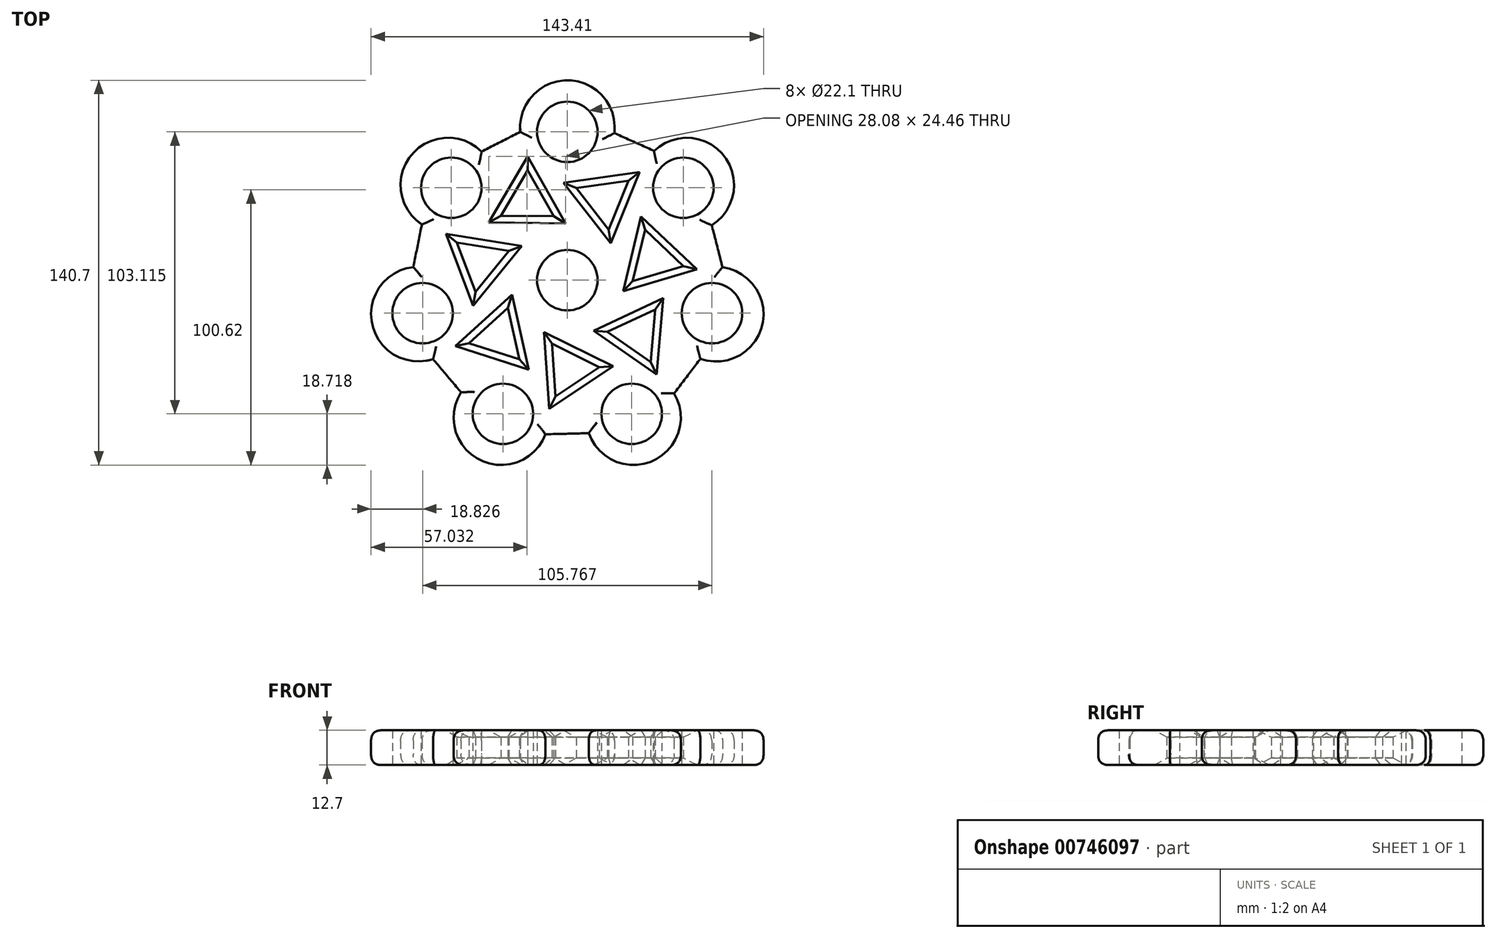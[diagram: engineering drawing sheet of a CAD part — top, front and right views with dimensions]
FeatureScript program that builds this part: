
annotation { "Feature Type Name" : "Feature", "Feature Type Description" : "" }
export const myFeature = defineFeature(function(context is Context, id is Id, definition is map)
    precondition{}
    {
        {
            var Q0;
            Q0=qCreatedBy(makeId("Top.planeOp"),FACE);
            var sketch = newSketch(context, id + "F0", { "sketchPlane" : qUnion([Q0])});
            skCircle(sketch, "E0", {"center": v(0, 0) * mm, "radius": 11.05 * mm});
            skCircle(sketch, "E1", {"center": v(0, 54.24) * mm, "radius": 11.05 * mm});
            skCircle(sketch, "E2.1.0", {"center": v(-42.4, 33.82) * mm, "radius": 11.05 * mm});
            skCircle(sketch, "E2.2.0", {"center": v(-52.88, -12.07) * mm, "radius": 11.05 * mm});
            skCircle(sketch, "E2.3.0", {"center": v(-23.54, -48.87) * mm, "radius": 11.05 * mm});
            skCircle(sketch, "E2.4.0", {"center": v(23.54, -48.87) * mm, "radius": 11.05 * mm});
            skCircle(sketch, "E2.5.0", {"center": v(52.88, -12.07) * mm, "radius": 11.05 * mm});
            skCircle(sketch, "E2.6.0", {"center": v(42.4, 33.82) * mm, "radius": 11.05 * mm});
            skArc(sketch, "E3", {"start": v(17.2, 53.8) * mm, "mid": v(0.24, 73.1) * mm, "end": v(-17.2, 54.24) * mm});
            skArc(sketch, "E4.1.0", {"start": v(-31.34, 47) * mm, "mid": v(-57, 45.77) * mm, "end": v(-53.14, 20.37) * mm});
            skArc(sketch, "E4.2.0", {"start": v(-56.29, 4.8) * mm, "mid": v(-71.33, -16.03) * mm, "end": v(-49.05, -28.85) * mm});
            skArc(sketch, "E4.3.0", {"start": v(-38.85, -41.01) * mm, "mid": v(-31.94, -65.76) * mm, "end": v(-8.03, -56.34) * mm});
            skArc(sketch, "E4.4.0", {"start": v(7.84, -55.95) * mm, "mid": v(31.5, -65.97) * mm, "end": v(39.04, -41.4) * mm});
            skArc(sketch, "E4.5.0", {"start": v(48.63, -28.75) * mm, "mid": v(71.22, -16.5) * mm, "end": v(56.71, 4.7) * mm});
            skArc(sketch, "E4.6.0", {"start": v(52.8, 20.1) * mm, "mid": v(57.3, 45.4) * mm, "end": v(31.68, 47.28) * mm});
            skLineSegment(sketch, "E5", {"start": v(-31.34, 47) * mm, "end": v(-17.2, 54.24) * mm});
            skLineSegment(sketch, "E6.1.0", {"start": v(-56.29, 4.8) * mm, "end": v(-53.14, 20.37) * mm});
            skLineSegment(sketch, "E6.2.0", {"start": v(-38.85, -41.01) * mm, "end": v(-49.05, -28.85) * mm});
            skLineSegment(sketch, "E6.3.0", {"start": v(7.84, -55.95) * mm, "end": v(-8.03, -56.34) * mm});
            skLineSegment(sketch, "E6.4.0", {"start": v(48.63, -28.75) * mm, "end": v(39.04, -41.4) * mm});
            skLineSegment(sketch, "E6.5.0", {"start": v(52.8, 20.1) * mm, "end": v(56.71, 4.7) * mm});
            skLineSegment(sketch, "E6.6.0", {"start": v(17.2, 53.8) * mm, "end": v(31.68, 47.28) * mm});
            skCircle(sketch, "E7.cCircle", {"center": v(-14.6, 29.05) * mm, "radius": 11.13 * mm, "construction": true});
            skLineSegment(sketch, "E7.0", {"start": v(-5.01, 23.38) * mm, "end": v(-24.3, 23.58) * mm});
            skLineSegment(sketch, "E7.1", {"start": v(-24.3, 23.58) * mm, "end": v(-14.48, 40.18) * mm});
            skLineSegment(sketch, "E7.2", {"start": v(-14.48, 40.18) * mm, "end": v(-5.01, 23.38) * mm});
            skLineSegment(sketch, "E8.1.0", {"start": v(-40.44, 13.73) * mm, "end": v(-21.4, 10.66) * mm});
            skLineSegment(sketch, "E8.1.1", {"start": v(-33.58, -4.3) * mm, "end": v(-40.44, 13.73) * mm});
            skLineSegment(sketch, "E8.1.2", {"start": v(-21.4, 10.66) * mm, "end": v(-33.58, -4.3) * mm});
            skLineSegment(sketch, "E8.2.0", {"start": v(-35.95, -23.06) * mm, "end": v(-21.68, -10.09) * mm});
            skLineSegment(sketch, "E8.2.1", {"start": v(-17.58, -28.93) * mm, "end": v(-35.95, -23.06) * mm});
            skLineSegment(sketch, "E8.2.2", {"start": v(-21.68, -10.09) * mm, "end": v(-17.58, -28.93) * mm});
            skLineSegment(sketch, "E8.3.0", {"start": v(-4.39, -42.49) * mm, "end": v(-5.63, -23.24) * mm});
            skLineSegment(sketch, "E8.3.1", {"start": v(11.66, -31.78) * mm, "end": v(-4.39, -42.49) * mm});
            skLineSegment(sketch, "E8.3.2", {"start": v(-5.63, -23.24) * mm, "end": v(11.66, -31.78) * mm});
            skLineSegment(sketch, "E8.4.0", {"start": v(30.48, -29.92) * mm, "end": v(14.66, -18.9) * mm});
            skLineSegment(sketch, "E8.4.1", {"start": v(32.12, -10.7) * mm, "end": v(30.48, -29.92) * mm});
            skLineSegment(sketch, "E8.4.2", {"start": v(14.66, -18.9) * mm, "end": v(32.12, -10.7) * mm});
            skLineSegment(sketch, "E8.5.0", {"start": v(42.4, 5.18) * mm, "end": v(23.91, -0.32) * mm});
            skLineSegment(sketch, "E8.5.1", {"start": v(28.4, 18.44) * mm, "end": v(42.4, 5.18) * mm});
            skLineSegment(sketch, "E8.5.2", {"start": v(23.91, -0.32) * mm, "end": v(28.4, 18.44) * mm});
            skLineSegment(sketch, "E8.6.0", {"start": v(22.38, 36.38) * mm, "end": v(15.16, 18.5) * mm});
            skLineSegment(sketch, "E8.6.1", {"start": v(3.29, 33.7) * mm, "end": v(22.38, 36.38) * mm});
            skLineSegment(sketch, "E8.6.2", {"start": v(15.16, 18.5) * mm, "end": v(3.29, 33.7) * mm});
            skSolve(sketch);
        }
        {
            var Q0;
            Q0=makeQuery(id+"F0.imprint","IMPRINT",FACE,{"disambiguationData":[TD([[makeQuery(id+"F0.imprint","IMPRINT",EDGE,{"derivedFrom":sQuery(id+"F0.wireOp",EDGE,"E0")}),-1.0]])]});
            extrude(context, id + "F1", {"entities" : qUnion([Q0]), "depth" : 12.7 * mm, "offsetDistance" : 25.4 * mm});
        }
        {
            var Q0;
            Q0=makeQuery(id+"F1.opExtrude","CAP_EDGE",EDGE,{"disambiguationData":[OSD([sQuery(id+"F0.wireOp",EDGE,"E6.3.0")])],"isStart":false});
            var Q1;
            Q1=makeQuery(id+"F1.opExtrude","CAP_EDGE",EDGE,{"disambiguationData":[OSD([sQuery(id+"F0.wireOp",EDGE,"E4.4.0")])],"isStart":false});
            var Q2;
            Q2=makeQuery(id+"F1.opExtrude","CAP_EDGE",EDGE,{"disambiguationData":[OSD([sQuery(id+"F0.wireOp",EDGE,"E6.4.0")])],"isStart":false});
            var Q3;
            Q3=makeQuery(id+"F1.opExtrude","CAP_EDGE",EDGE,{"disambiguationData":[OSD([sQuery(id+"F0.wireOp",EDGE,"E4.5.0")])],"isStart":false});
            var Q4;
            Q4=makeQuery(id+"F1.opExtrude","CAP_EDGE",EDGE,{"disambiguationData":[OSD([sQuery(id+"F0.wireOp",EDGE,"E6.5.0")])],"isStart":false});
            var Q5;
            Q5=makeQuery(id+"F1.opExtrude","CAP_EDGE",EDGE,{"disambiguationData":[OSD([sQuery(id+"F0.wireOp",EDGE,"E4.6.0")])],"isStart":false});
            var Q6;
            Q6=makeQuery(id+"F1.opExtrude","CAP_EDGE",EDGE,{"disambiguationData":[OSD([sQuery(id+"F0.wireOp",EDGE,"E6.6.0")])],"isStart":false});
            var Q7;
            Q7=makeQuery(id+"F1.opExtrude","CAP_EDGE",EDGE,{"disambiguationData":[OSD([sQuery(id+"F0.wireOp",EDGE,"E3")])],"isStart":false});
            var Q8;
            Q8=makeQuery(id+"F1.opExtrude","CAP_EDGE",EDGE,{"disambiguationData":[OSD([sQuery(id+"F0.wireOp",EDGE,"E5")])],"isStart":false});
            var Q9;
            Q9=makeQuery(id+"F1.opExtrude","CAP_EDGE",EDGE,{"disambiguationData":[OSD([sQuery(id+"F0.wireOp",EDGE,"E4.1.0")])],"isStart":false});
            var Q10;
            Q10=makeQuery(id+"F1.opExtrude","CAP_EDGE",EDGE,{"disambiguationData":[OSD([sQuery(id+"F0.wireOp",EDGE,"E6.1.0")])],"isStart":false});
            var Q11;
            Q11=makeQuery(id+"F1.opExtrude","CAP_EDGE",EDGE,{"disambiguationData":[OSD([sQuery(id+"F0.wireOp",EDGE,"E4.2.0")])],"isStart":false});
            var Q12;
            Q12=makeQuery(id+"F1.opExtrude","CAP_EDGE",EDGE,{"disambiguationData":[OSD([sQuery(id+"F0.wireOp",EDGE,"E6.2.0")])],"isStart":false});
            var Q13;
            Q13=makeQuery(id+"F1.opExtrude","CAP_EDGE",EDGE,{"disambiguationData":[OSD([sQuery(id+"F0.wireOp",EDGE,"E4.3.0")])],"isStart":false});
            var Q14;
            Q14=makeQuery(id+"F1.opExtrude","CAP_EDGE",EDGE,{"disambiguationData":[OSD([sQuery(id+"F0.wireOp",EDGE,"E3")])],"isStart":true});
            var Q15;
            Q15=makeQuery(id+"F1.opExtrude","CAP_EDGE",EDGE,{"disambiguationData":[OSD([sQuery(id+"F0.wireOp",EDGE,"E6.6.0")])],"isStart":true});
            var Q16;
            Q16=makeQuery(id+"F1.opExtrude","CAP_EDGE",EDGE,{"disambiguationData":[OSD([sQuery(id+"F0.wireOp",EDGE,"E4.6.0")])],"isStart":true});
            var Q17;
            Q17=makeQuery(id+"F1.opExtrude","CAP_EDGE",EDGE,{"disambiguationData":[OSD([sQuery(id+"F0.wireOp",EDGE,"E6.5.0")])],"isStart":true});
            var Q18;
            Q18=makeQuery(id+"F1.opExtrude","CAP_EDGE",EDGE,{"disambiguationData":[OSD([sQuery(id+"F0.wireOp",EDGE,"E4.5.0")])],"isStart":true});
            var Q19;
            Q19=makeQuery(id+"F1.opExtrude","CAP_EDGE",EDGE,{"disambiguationData":[OSD([sQuery(id+"F0.wireOp",EDGE,"E6.4.0")])],"isStart":true});
            var Q20;
            Q20=makeQuery(id+"F1.opExtrude","CAP_EDGE",EDGE,{"disambiguationData":[OSD([sQuery(id+"F0.wireOp",EDGE,"E4.4.0")])],"isStart":true});
            var Q21;
            Q21=makeQuery(id+"F1.opExtrude","CAP_EDGE",EDGE,{"disambiguationData":[OSD([sQuery(id+"F0.wireOp",EDGE,"E4.3.0")])],"isStart":true});
            var Q22;
            Q22=makeQuery(id+"F1.opExtrude","CAP_EDGE",EDGE,{"disambiguationData":[OSD([sQuery(id+"F0.wireOp",EDGE,"E6.3.0")])],"isStart":true});
            var Q23;
            Q23=makeQuery(id+"F1.opExtrude","CAP_EDGE",EDGE,{"disambiguationData":[OSD([sQuery(id+"F0.wireOp",EDGE,"E6.2.0")])],"isStart":true});
            var Q24;
            Q24=makeQuery(id+"F1.opExtrude","CAP_EDGE",EDGE,{"disambiguationData":[OSD([sQuery(id+"F0.wireOp",EDGE,"E4.2.0")])],"isStart":true});
            var Q25;
            Q25=makeQuery(id+"F1.opExtrude","CAP_EDGE",EDGE,{"disambiguationData":[OSD([sQuery(id+"F0.wireOp",EDGE,"E4.1.0")])],"isStart":true});
            var Q26;
            Q26=makeQuery(id+"F1.opExtrude","CAP_EDGE",EDGE,{"disambiguationData":[OSD([sQuery(id+"F0.wireOp",EDGE,"E6.1.0")])],"isStart":true});
            var Q27;
            Q27=makeQuery(id+"F1.opExtrude","CAP_EDGE",EDGE,{"disambiguationData":[OSD([sQuery(id+"F0.wireOp",EDGE,"E5")])],"isStart":true});
            fillet(context, id + "F2", {"entities" : qUnion([Q0, Q1, Q2, Q3, Q4, Q5, Q6, Q7, Q8, Q9, Q10, Q11, Q12, Q13, Q14, Q15, Q16, Q17, Q18, Q19, Q20, Q21, Q22, Q23, Q24, Q25, Q26, Q27]), "radius" : 3.8 * mm, "tangentPropagation" : true, "rho" : 0.5, "crossSection" : FilletCrossSection.CONIC, "allowEdgeOverflow" : false});
        }
        {
            var Q0;
            Q0=makeQuery(id+"F1.opExtrude","CAP_EDGE",EDGE,{"disambiguationData":[OSD([sQuery(id+"F0.wireOp",EDGE,"E8.1.0")])],"isStart":false});
            var Q1;
            Q1=makeQuery(id+"F1.opExtrude","CAP_EDGE",EDGE,{"disambiguationData":[OSD([sQuery(id+"F0.wireOp",EDGE,"E8.1.2")])],"isStart":false});
            var Q2;
            Q2=makeQuery(id+"F1.opExtrude","CAP_EDGE",EDGE,{"disambiguationData":[OSD([sQuery(id+"F0.wireOp",EDGE,"E8.1.1")])],"isStart":false});
            var Q3;
            Q3=makeQuery(id+"F1.opExtrude","CAP_EDGE",EDGE,{"disambiguationData":[OSD([sQuery(id+"F0.wireOp",EDGE,"E7.2")])],"isStart":false});
            var Q4;
            Q4=makeQuery(id+"F1.opExtrude","CAP_EDGE",EDGE,{"disambiguationData":[OSD([sQuery(id+"F0.wireOp",EDGE,"E7.1")])],"isStart":false});
            var Q5;
            Q5=makeQuery(id+"F1.opExtrude","CAP_EDGE",EDGE,{"disambiguationData":[OSD([sQuery(id+"F0.wireOp",EDGE,"E7.0")])],"isStart":false});
            var Q6;
            Q6=makeQuery(id+"F1.opExtrude","CAP_EDGE",EDGE,{"disambiguationData":[OSD([sQuery(id+"F0.wireOp",EDGE,"E8.6.1")])],"isStart":false});
            var Q7;
            Q7=makeQuery(id+"F1.opExtrude","CAP_EDGE",EDGE,{"disambiguationData":[OSD([sQuery(id+"F0.wireOp",EDGE,"E8.6.0")])],"isStart":false});
            var Q8;
            Q8=makeQuery(id+"F1.opExtrude","CAP_EDGE",EDGE,{"disambiguationData":[OSD([sQuery(id+"F0.wireOp",EDGE,"E8.6.2")])],"isStart":false});
            var Q9;
            Q9=makeQuery(id+"F1.opExtrude","CAP_EDGE",EDGE,{"disambiguationData":[OSD([sQuery(id+"F0.wireOp",EDGE,"E8.5.2")])],"isStart":false});
            var Q10;
            Q10=makeQuery(id+"F1.opExtrude","CAP_EDGE",EDGE,{"disambiguationData":[OSD([sQuery(id+"F0.wireOp",EDGE,"E8.5.1")])],"isStart":false});
            var Q11;
            Q11=makeQuery(id+"F1.opExtrude","CAP_EDGE",EDGE,{"disambiguationData":[OSD([sQuery(id+"F0.wireOp",EDGE,"E8.5.0")])],"isStart":false});
            var Q12;
            Q12=makeQuery(id+"F1.opExtrude","CAP_EDGE",EDGE,{"disambiguationData":[OSD([sQuery(id+"F0.wireOp",EDGE,"E8.4.2")])],"isStart":false});
            var Q13;
            Q13=makeQuery(id+"F1.opExtrude","CAP_EDGE",EDGE,{"disambiguationData":[OSD([sQuery(id+"F0.wireOp",EDGE,"E8.4.1")])],"isStart":false});
            var Q14;
            Q14=makeQuery(id+"F1.opExtrude","CAP_EDGE",EDGE,{"disambiguationData":[OSD([sQuery(id+"F0.wireOp",EDGE,"E8.4.0")])],"isStart":false});
            var Q15;
            Q15=makeQuery(id+"F1.opExtrude","CAP_EDGE",EDGE,{"disambiguationData":[OSD([sQuery(id+"F0.wireOp",EDGE,"E8.3.1")])],"isStart":false});
            var Q16;
            Q16=makeQuery(id+"F1.opExtrude","CAP_EDGE",EDGE,{"disambiguationData":[OSD([sQuery(id+"F0.wireOp",EDGE,"E8.3.2")])],"isStart":false});
            var Q17;
            Q17=makeQuery(id+"F1.opExtrude","CAP_EDGE",EDGE,{"disambiguationData":[OSD([sQuery(id+"F0.wireOp",EDGE,"E8.3.0")])],"isStart":false});
            var Q18;
            Q18=makeQuery(id+"F1.opExtrude","CAP_EDGE",EDGE,{"disambiguationData":[OSD([sQuery(id+"F0.wireOp",EDGE,"E8.2.1")])],"isStart":false});
            var Q19;
            Q19=makeQuery(id+"F1.opExtrude","CAP_EDGE",EDGE,{"disambiguationData":[OSD([sQuery(id+"F0.wireOp",EDGE,"E8.2.0")])],"isStart":false});
            var Q20;
            Q20=makeQuery(id+"F1.opExtrude","CAP_EDGE",EDGE,{"disambiguationData":[OSD([sQuery(id+"F0.wireOp",EDGE,"E8.2.2")])],"isStart":false});
            var Q21;
            Q21=makeQuery(id+"F1.opExtrude","CAP_EDGE",EDGE,{"disambiguationData":[OSD([sQuery(id+"F0.wireOp",EDGE,"E8.3.2")])],"isStart":true});
            var Q22;
            Q22=makeQuery(id+"F1.opExtrude","CAP_EDGE",EDGE,{"disambiguationData":[OSD([sQuery(id+"F0.wireOp",EDGE,"E8.3.0")])],"isStart":true});
            var Q23;
            Q23=makeQuery(id+"F1.opExtrude","CAP_EDGE",EDGE,{"disambiguationData":[OSD([sQuery(id+"F0.wireOp",EDGE,"E8.3.1")])],"isStart":true});
            var Q24;
            Q24=makeQuery(id+"F1.opExtrude","CAP_EDGE",EDGE,{"disambiguationData":[OSD([sQuery(id+"F0.wireOp",EDGE,"E8.4.0")])],"isStart":true});
            var Q25;
            Q25=makeQuery(id+"F1.opExtrude","CAP_EDGE",EDGE,{"disambiguationData":[OSD([sQuery(id+"F0.wireOp",EDGE,"E8.4.1")])],"isStart":true});
            var Q26;
            Q26=makeQuery(id+"F1.opExtrude","CAP_EDGE",EDGE,{"disambiguationData":[OSD([sQuery(id+"F0.wireOp",EDGE,"E8.4.2")])],"isStart":true});
            var Q27;
            Q27=makeQuery(id+"F1.opExtrude","CAP_EDGE",EDGE,{"disambiguationData":[OSD([sQuery(id+"F0.wireOp",EDGE,"E8.5.1")])],"isStart":true});
            var Q28;
            Q28=makeQuery(id+"F1.opExtrude","CAP_EDGE",EDGE,{"disambiguationData":[OSD([sQuery(id+"F0.wireOp",EDGE,"E8.5.0")])],"isStart":true});
            var Q29;
            Q29=makeQuery(id+"F1.opExtrude","CAP_EDGE",EDGE,{"disambiguationData":[OSD([sQuery(id+"F0.wireOp",EDGE,"E8.5.2")])],"isStart":true});
            var Q30;
            Q30=makeQuery(id+"F1.opExtrude","CAP_EDGE",EDGE,{"disambiguationData":[OSD([sQuery(id+"F0.wireOp",EDGE,"E8.6.1")])],"isStart":true});
            var Q31;
            Q31=makeQuery(id+"F1.opExtrude","CAP_EDGE",EDGE,{"disambiguationData":[OSD([sQuery(id+"F0.wireOp",EDGE,"E8.6.2")])],"isStart":true});
            var Q32;
            Q32=makeQuery(id+"F1.opExtrude","CAP_EDGE",EDGE,{"disambiguationData":[OSD([sQuery(id+"F0.wireOp",EDGE,"E8.6.0")])],"isStart":true});
            var Q33;
            Q33=makeQuery(id+"F1.opExtrude","CAP_EDGE",EDGE,{"disambiguationData":[OSD([sQuery(id+"F0.wireOp",EDGE,"E7.2")])],"isStart":true});
            var Q34;
            Q34=makeQuery(id+"F1.opExtrude","CAP_EDGE",EDGE,{"disambiguationData":[OSD([sQuery(id+"F0.wireOp",EDGE,"E7.1")])],"isStart":true});
            var Q35;
            Q35=makeQuery(id+"F1.opExtrude","CAP_EDGE",EDGE,{"disambiguationData":[OSD([sQuery(id+"F0.wireOp",EDGE,"E7.0")])],"isStart":true});
            var Q36;
            Q36=makeQuery(id+"F1.opExtrude","CAP_EDGE",EDGE,{"disambiguationData":[OSD([sQuery(id+"F0.wireOp",EDGE,"E8.1.0")])],"isStart":true});
            var Q37;
            Q37=makeQuery(id+"F1.opExtrude","CAP_EDGE",EDGE,{"disambiguationData":[OSD([sQuery(id+"F0.wireOp",EDGE,"E8.1.1")])],"isStart":true});
            var Q38;
            Q38=makeQuery(id+"F1.opExtrude","CAP_EDGE",EDGE,{"disambiguationData":[OSD([sQuery(id+"F0.wireOp",EDGE,"E8.1.2")])],"isStart":true});
            var Q39;
            Q39=makeQuery(id+"F1.opExtrude","CAP_EDGE",EDGE,{"disambiguationData":[OSD([sQuery(id+"F0.wireOp",EDGE,"E8.2.0")])],"isStart":true});
            var Q40;
            Q40=makeQuery(id+"F1.opExtrude","CAP_EDGE",EDGE,{"disambiguationData":[OSD([sQuery(id+"F0.wireOp",EDGE,"E8.2.1")])],"isStart":true});
            var Q41;
            Q41=makeQuery(id+"F1.opExtrude","CAP_EDGE",EDGE,{"disambiguationData":[OSD([sQuery(id+"F0.wireOp",EDGE,"E8.2.2")])],"isStart":true});
            chamfer(context, id + "F3", {"entities" : qUnion([Q0, Q1, Q2, Q3, Q4, Q5, Q6, Q7, Q8, Q9, Q10, Q11, Q12, Q13, Q14, Q15, Q16, Q17, Q18, Q19, Q20, Q21, Q22, Q23, Q24, Q25, Q26, Q27, Q28, Q29, Q30, Q31, Q32, Q33, Q34, Q35, Q36, Q37, Q38, Q39, Q40, Q41]), "width" : 2.54 * mm, "tangentPropagation" : true});
        }
    });
